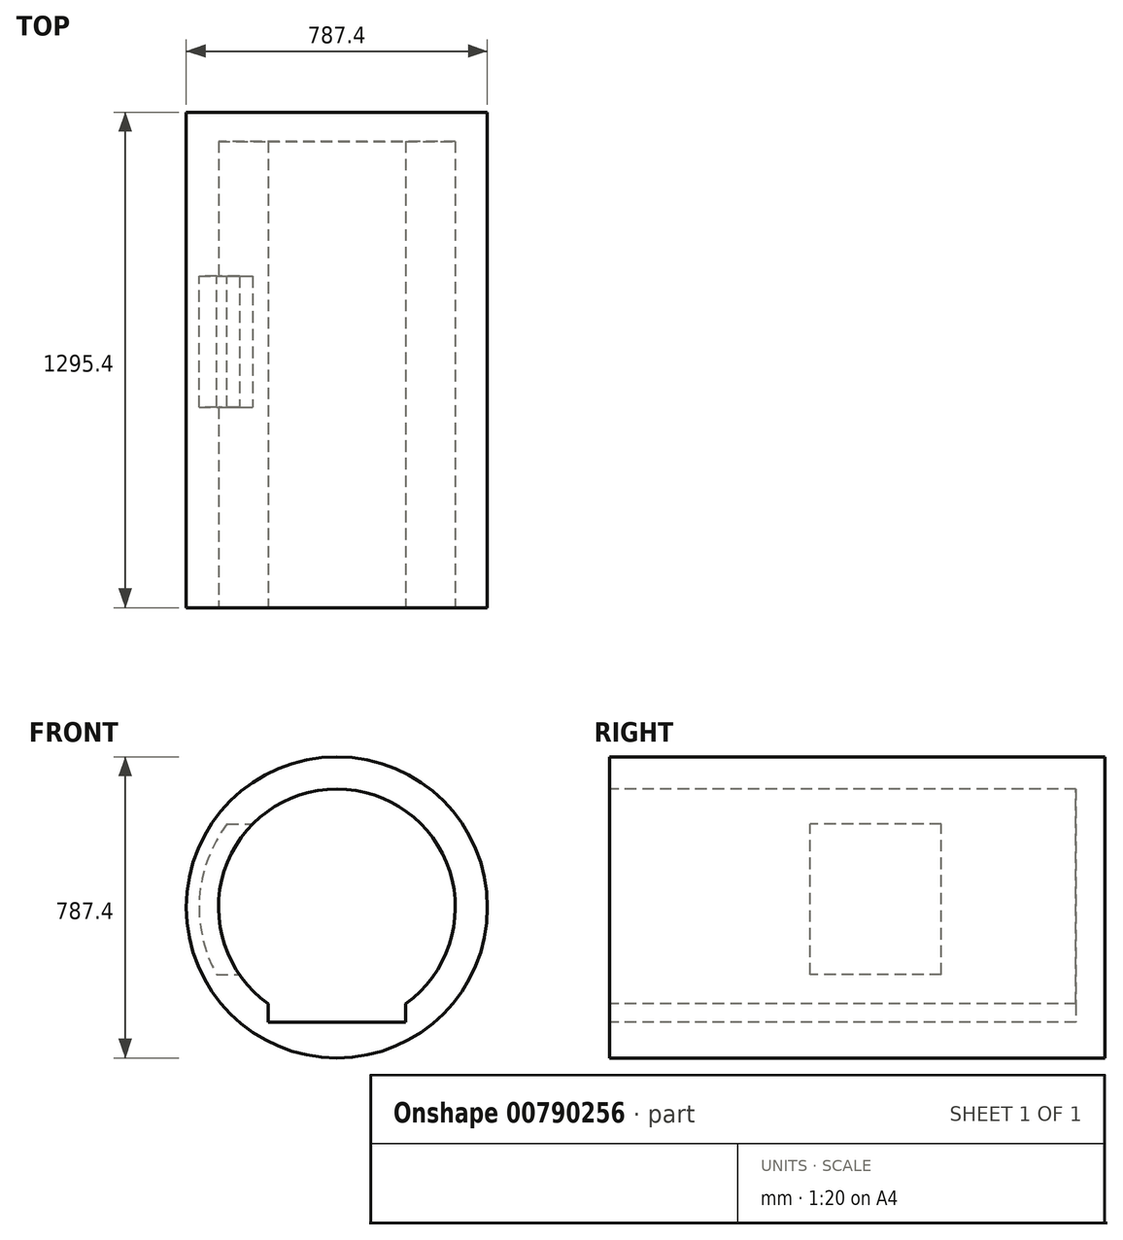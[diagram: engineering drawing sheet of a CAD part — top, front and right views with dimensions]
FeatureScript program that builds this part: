
annotation { "Feature Type Name" : "Feature", "Feature Type Description" : "" }
export const myFeature = defineFeature(function(context is Context, id is Id, definition is map)
    precondition{}
    {
        {
            var Q0;
            Q0=qCreatedBy(makeId("Front.planeOp"),FACE);
            var sketch = newSketch(context, id + "F0", { "sketchPlane" : qUnion([Q0])});
            skCircle(sketch, "E0", {"center": v(0, 0) * mm, "radius": 360.36 * mm});
            skPoint(sketch, "E1.middle", {"position": v(0, -253.46) * mm});
            skSolve(sketch);
        }
        {
            var Q0;
            {var subQ5=sQuery(id+"F0.wireOp",EDGE,"E1.top");Q0=makeQuery(id+"F0.imprint","IMPRINT",FACE,{"disambiguationData":[TD([[makeQuery(id+"F0.imprint","IMPRINT",EDGE,{"derivedFrom":subQ5}),-1.0]])]});}
            var Q1;
            Q1=makeQuery(id+"F0.imprint","IMPRINT",FACE,{"disambiguationData":[TD([[makeQuery(id+"F0.imprint","IMPRINT",EDGE,{"derivedFrom":sQuery(id+"F0.wireOp",EDGE,"E0")}),1.0]])]});
            var Q2;
            {var subQ5=sQuery(id+"F0.wireOp",EDGE,"E1.top");Q2=makeQuery(id+"F0.imprint","IMPRINT",FACE,{"disambiguationData":[TD([[makeQuery(id+"F0.imprint","IMPRINT",EDGE,{"derivedFrom":subQ5}),1.0]])]});}
            var Q3;
            {var subQ5=sQuery(id+"F0.wireOp",EDGE,"E1.bottom");Q3=makeQuery(id+"F0.imprint","IMPRINT",FACE,{"disambiguationData":[TD([[makeQuery(id+"F0.imprint","IMPRINT",EDGE,{"derivedFrom":subQ5}),-1.0]])]});}
            extrude(context, id + "F1", {"entities" : qUnion([Q0, Q1, Q2, Q3]), "depth" : 1295.4 * mm, "offsetDistance" : 25.4 * mm, "symmetric" : true});
        }
        {
            var Q0;
            Q0=makeQuery(id+"F1.opExtrude","CAP_FACE",FACE,{"disambiguationData":[OSD([sQuery(id+"F0.wireOp",EDGE,"E0")])],"isStart":false});
            var sketch = newSketch(context, id + "F2", { "sketchPlane" : qUnion([Q0])});
            skCircle(sketch, "E2", {"center": v(0, 0) * mm, "radius": 309.56 * mm});
            skLineSegment(sketch, "E3", {"start": v(-179.78, -252) * mm, "end": v(-179.78, -300.04) * mm});
            skLineSegment(sketch, "E4", {"start": v(179.77, -252.02) * mm, "end": v(179.77, -300.04) * mm});
            skLineSegment(sketch, "E5", {"start": v(-179.78, -300.04) * mm, "end": v(179.77, -300.04) * mm});
            skSolve(sketch);
        }
        {
            var Q0;
            {var subQ0=sQuery(id+"F2.wireOp",EDGE,"E3");Q0=makeQuery(id+"F2.imprint","IMPRINT",FACE,{"disambiguationData":[TD([[makeQuery(id+"F2.imprint","IMPRINT",EDGE,{"derivedFrom":subQ0}),1.0]])]});}
            var Q1;
            {var subQ0=sQuery(id+"F2.wireOp",EDGE,"E2");var subQ1=makeQuery(id+"F2.imprint","INTERSECT",VERTEX,{"derivedFrom":[subQ0,sQuery(id+"F2.wireOp",EDGE,"E3")]});Q1=makeQuery(id+"F2.imprint","IMPRINT",FACE,{"disambiguationData":[TD([[makeQuery(id+"F2.imprint","IMPRINT",EDGE,{"disambiguationData":[TD([[subQ1,-1.0]])],"derivedFrom":subQ0}),1.0]])]});}
            var Q2;
            {var subQ0=sQuery(id+"F2.wireOp",EDGE,"E4");Q2=makeQuery(id+"F2.imprint","IMPRINT",FACE,{"disambiguationData":[TD([[makeQuery(id+"F2.imprint","IMPRINT",EDGE,{"derivedFrom":subQ0}),-1.0]])]});}
            extrude(context, id + "F3", {"entities" : qUnion([Q0, Q1, Q2]), "operationType" : NewBodyOperationType.REMOVE, "oppositeDirection" : true, "depth" : 1219.2 * mm, "offsetDistance" : 25.4 * mm});
        }
        {
            var Q0;
            Q0=qCreatedBy(makeId("Right.planeOp"),FACE);
            cPlane(context, id + "F4", {"entities" : qUnion([Q0]), "cplaneType" : CPlaneType.OFFSET, "offset" : 203.2 * mm, "oppositeDirection" : true, "width" : 152.4 * mm, "height" : 152.4 * mm});
        }
        {
            var Q0;
            Q0=qCreatedBy(id+"F4.planeOp",FACE);
            var sketch = newSketch(context, id + "F5", { "sketchPlane" : qUnion([Q0])});
            skLineSegment(sketch, "E6.bottom", {"start": v(219.07, -175.8) * mm, "end": v(-123.83, -175.8) * mm});
            skLineSegment(sketch, "E6.top", {"start": v(219.07, 217.9) * mm, "end": v(-123.83, 217.9) * mm});
            skLineSegment(sketch, "E6.left", {"start": v(219.07, -175.8) * mm, "end": v(219.07, 217.9) * mm});
            skLineSegment(sketch, "E6.right", {"start": v(-123.83, -175.8) * mm, "end": v(-123.83, 217.9) * mm});
            skPoint(sketch, "E6.middle", {"position": v(47.62, 21.04) * mm});
            skSolve(sketch);
        }
        {
            var Q0;
            Q0=makeQuery(id+"F5.imprint","IMPRINT",FACE,{"disambiguationData":[TD([[makeQuery(id+"F5.imprint","IMPRINT",EDGE,{"derivedFrom":sQuery(id+"F5.wireOp",EDGE,"E6.bottom")}),-1.0]])]});
            extrude(context, id + "F6", {"entities" : qUnion([Q0]), "operationType" : NewBodyOperationType.REMOVE, "oppositeDirection" : true, "depth" : 279.4 * mm, "offsetDistance" : 25.4 * mm});
        }
        {
            var Q0;
            Q0=qCreatedBy(makeId("Front.planeOp"),FACE);
            var sketch = newSketch(context, id + "F7", { "sketchPlane" : qUnion([Q0])});
            skCircle(sketch, "E7", {"center": v(0, 0) * mm, "radius": 360.36 * mm});
            skCircle(sketch, "E8", {"center": v(0, 0) * mm, "radius": 393.7 * mm});
            skSolve(sketch);
        }
        {
            var Q0;
            Q0=makeQuery(id+"F7.imprint","IMPRINT",FACE,{"disambiguationData":[TD([[makeQuery(id+"F7.imprint","IMPRINT",EDGE,{"derivedFrom":sQuery(id+"F7.wireOp",EDGE,"E7")}),-1.0]])]});
            extrude(context, id + "F8", {"entities" : qUnion([Q0]), "operationType" : NewBodyOperationType.ADD, "depth" : 1295.4 * mm, "offsetDistance" : 25.4 * mm, "symmetric" : true});
        }
        {
            var Q0;
            Q0=qCreatedBy(id+"F4.planeOp",FACE);
            cPlane(context, id + "F9", {"entities" : qUnion([Q0]), "cplaneType" : CPlaneType.OFFSET, "offset" : 127 * mm, "oppositeDirection" : true, "width" : 152.4 * mm, "height" : 152.4 * mm});
        }
    });
